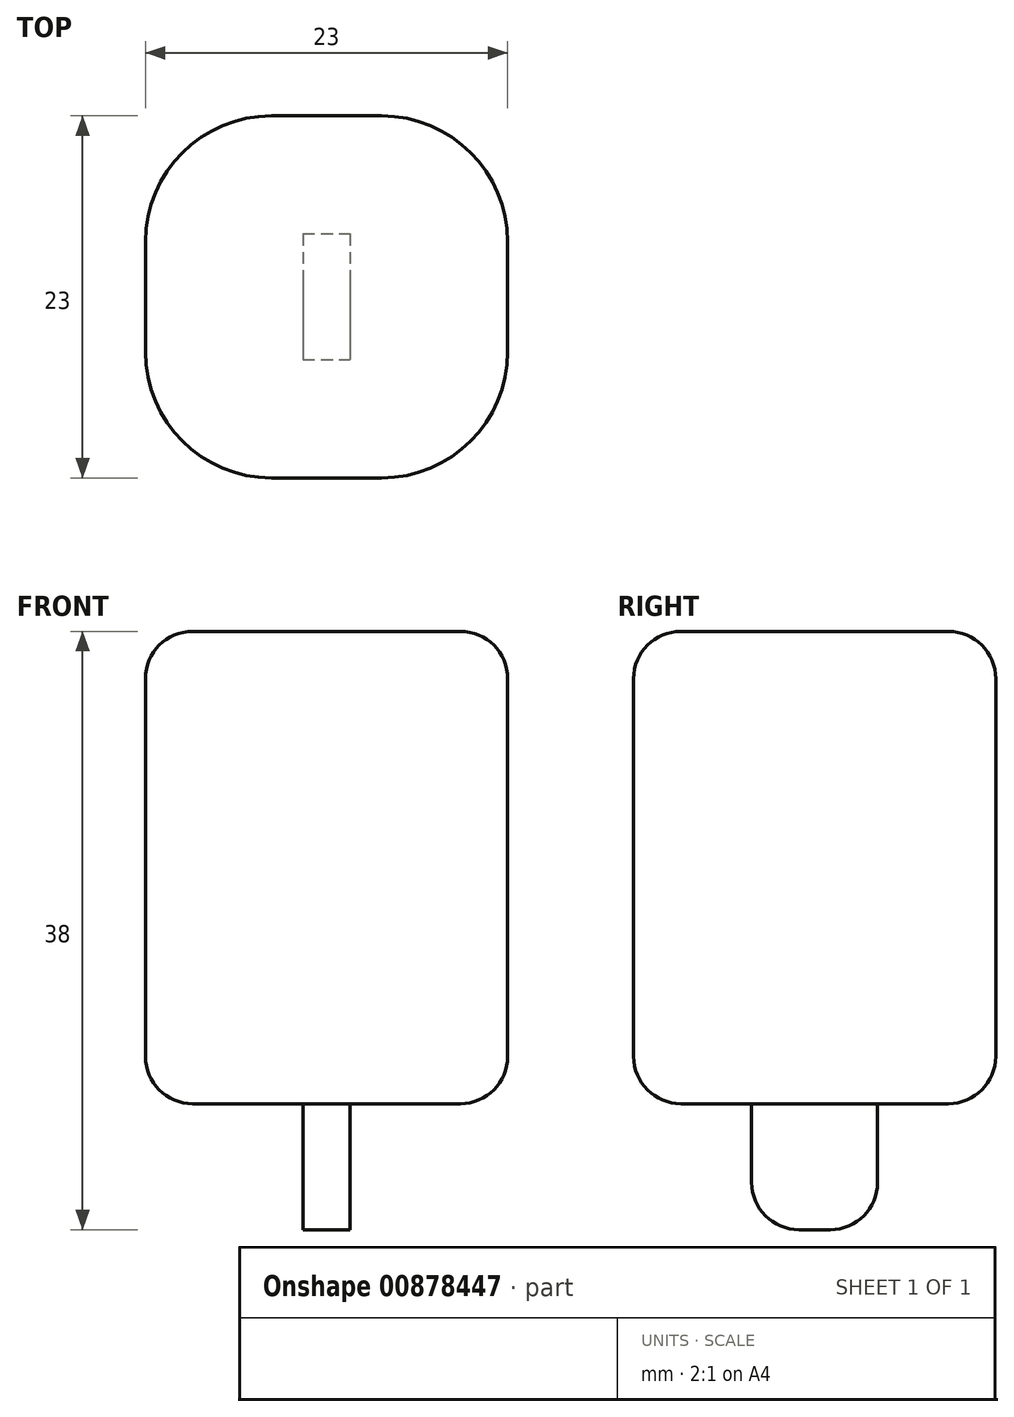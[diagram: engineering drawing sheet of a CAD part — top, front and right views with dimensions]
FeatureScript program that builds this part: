
annotation { "Feature Type Name" : "Feature", "Feature Type Description" : "" }
export const myFeature = defineFeature(function(context is Context, id is Id, definition is map)
    precondition{}
    {
        {
            var Q0;
            Q0=qCreatedBy(makeId("Top.planeOp"),FACE);
            var sketch = newSketch(context, id + "F0", { "sketchPlane" : qUnion([Q0])});
            skLineSegment(sketch, "E0.bottom", {"start": v(3.5, 11.5) * mm, "end": v(-3.5, 11.5) * mm});
            skLineSegment(sketch, "E0.top", {"start": v(3.5, -11.5) * mm, "end": v(-3.5, -11.5) * mm});
            skLineSegment(sketch, "E0.left", {"start": v(11.5, 3.5) * mm, "end": v(11.5, -3.5) * mm});
            skLineSegment(sketch, "E0.right", {"start": v(-11.5, 3.5) * mm, "end": v(-11.5, -3.5) * mm});
            skPoint(sketch, "E0.middle", {"position": v(0, 0) * mm});
            skPoint(sketch, "E1.visualSharp", {"position": v(-11.5, 11.5) * mm});
            skArc(sketch, "E1.filletArc", {"start": v(-3.5, 11.5) * mm, "mid": v(-9.16, 9.16) * mm, "end": v(-11.5, 3.5) * mm});
            skPoint(sketch, "E2.visualSharp", {"position": v(11.5, 11.5) * mm});
            skArc(sketch, "E2.filletArc", {"start": v(11.5, 3.5) * mm, "mid": v(9.16, 9.16) * mm, "end": v(3.5, 11.5) * mm});
            skPoint(sketch, "E3.visualSharp", {"position": v(11.5, -11.5) * mm});
            skArc(sketch, "E3.filletArc", {"start": v(3.5, -11.5) * mm, "mid": v(9.16, -9.16) * mm, "end": v(11.5, -3.5) * mm});
            skPoint(sketch, "E4.visualSharp", {"position": v(-11.5, -11.5) * mm});
            skArc(sketch, "E4.filletArc", {"start": v(-11.5, -3.5) * mm, "mid": v(-9.16, -9.16) * mm, "end": v(-3.5, -11.5) * mm});
            skSolve(sketch);
        }
        {
            var Q0;
            Q0 = qSketchRegion(id + "F0", true);
            extrude(context, id + "F1", {"entities" : qUnion([Q0]), "depth" : 30 * mm, "offsetDistance" : 25 * mm});
        }
        {
            var Q0;
            Q0=qCreatedBy(makeId("Top.planeOp"),FACE);
            var sketch = newSketch(context, id + "F2", { "sketchPlane" : qUnion([Q0])});
            skLineSegment(sketch, "E5.bottom", {"start": v(-1.5, 4) * mm, "end": v(1.5, 4) * mm});
            skLineSegment(sketch, "E5.top", {"start": v(-1.5, -4) * mm, "end": v(1.5, -4) * mm});
            skLineSegment(sketch, "E5.left", {"start": v(-1.5, 4) * mm, "end": v(-1.5, -4) * mm});
            skLineSegment(sketch, "E5.right", {"start": v(1.5, 4) * mm, "end": v(1.5, -4) * mm});
            skPoint(sketch, "E5.middle", {"position": v(0, 0) * mm});
            skSolve(sketch);
        }
        {
            var Q0;
            Q0 = qSketchRegion(id + "F2", true);
            extrude(context, id + "F3", {"entities" : qUnion([Q0]), "operationType" : NewBodyOperationType.ADD, "oppositeDirection" : true, "depth" : 8 * mm, "offsetDistance" : 25 * mm});
        }
        {
            var Q0;
            Q0=makeQuery(id+"F1.opExtrude","CAP_EDGE",EDGE,{"disambiguationData":[OSD([sQuery(id+"F0.wireOp",EDGE,"E4.filletArc")])],"isStart":false});
            var Q1;
            Q1=makeQuery(id+"F1.opExtrude","CAP_EDGE",EDGE,{"disambiguationData":[OSD([sQuery(id+"F0.wireOp",EDGE,"E3.filletArc")])],"isStart":true});
            var Q2;
            Q2=makeQuery(id+"F3.opExtrude","CAP_EDGE",EDGE,{"disambiguationData":[OSD([sQuery(id+"F2.wireOp",EDGE,"E5.left")])],"isStart":true});
            var Q3;
            Q3=makeQuery(id+"F3.opExtrude","CAP_EDGE",EDGE,{"disambiguationData":[OSD([sQuery(id+"F2.wireOp",EDGE,"E5.top")])],"isStart":true});
            var Q4;
            Q4=makeQuery(id+"F3.opExtrude","CAP_EDGE",EDGE,{"disambiguationData":[OSD([sQuery(id+"F2.wireOp",EDGE,"E5.right")])],"isStart":true});
            var Q5;
            Q5=makeQuery(id+"F3.opExtrude","CAP_EDGE",EDGE,{"disambiguationData":[OSD([sQuery(id+"F2.wireOp",EDGE,"E5.bottom")])],"isStart":true});
            var Q6;
            Q6=makeQuery(id+"F3.opExtrude","CAP_EDGE",EDGE,{"disambiguationData":[OSD([sQuery(id+"F2.wireOp",EDGE,"E5.bottom")])],"isStart":false});
            var Q7;
            Q7=makeQuery(id+"F3.opExtrude","CAP_EDGE",EDGE,{"disambiguationData":[OSD([sQuery(id+"F2.wireOp",EDGE,"E5.top")])],"isStart":false});
            fillet(context, id + "F4", {"entities" : qUnion([Q0, Q1, Q2, Q3, Q4, Q5, Q6, Q7]), "radius" : 3 * mm, "tangentPropagation" : true, "allowEdgeOverflow" : false});
        }
    });
